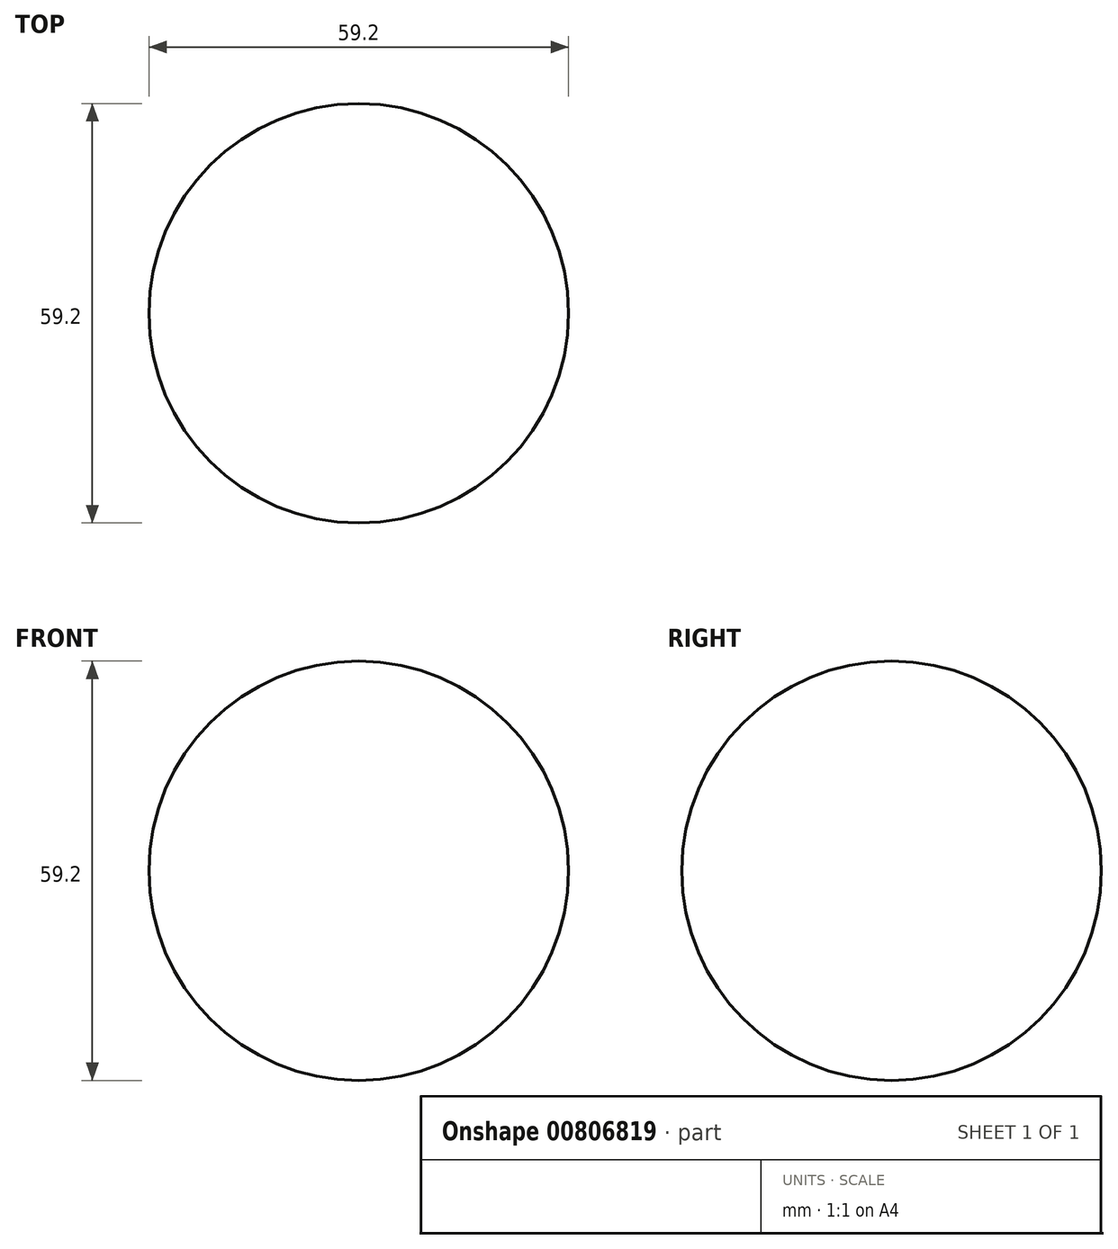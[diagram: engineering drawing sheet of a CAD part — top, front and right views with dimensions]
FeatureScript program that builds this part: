
annotation { "Feature Type Name" : "Feature", "Feature Type Description" : "" }
export const myFeature = defineFeature(function(context is Context, id is Id, definition is map)
    precondition{}
    {
        {
            var Q0;
            Q0=qCreatedBy(makeId("Front.planeOp"),FACE);
            var sketch = newSketch(context, id + "F0", { "sketchPlane" : qUnion([Q0])});
            skCircle(sketch, "E0", {"center": v(0, 0) * mm, "radius": 29.6 * mm});
            skLineSegment(sketch, "E1", {"start": v(0, 57.66) * mm, "end": v(0, -53.1) * mm});
            skSolve(sketch);
        }
        {
            var Q0;
            {var subQ0=sQuery(id+"F0.wireOp",EDGE,"E1");var subQ1=sQuery(id+"F0.wireOp",EDGE,"E0");var subQ2=makeQuery(id+"F0.imprint","INTERSECT",VERTEX,{"disambiguationData":[OD(0.0)],"derivedFrom":[subQ1,subQ0]});Q0=makeQuery(id+"F0.imprint","IMPRINT",FACE,{"disambiguationData":[TD([[makeQuery(id+"F0.imprint","IMPRINT",EDGE,{"disambiguationData":[TD([[subQ2,1.0]])],"derivedFrom":subQ1}),1.0]])]});}
            var Q1;
            Q1=sQuery(id+"F0.wireOp",EDGE,"E1");
            revolve(context, id + "F1", {"surfaceOperationType" : NewSurfaceOperationType.NEW, "entities" : qUnion([Q0]), "axis" : qUnion([Q1]), "revolveType" : RevolveType.FULL});
        }
    });
